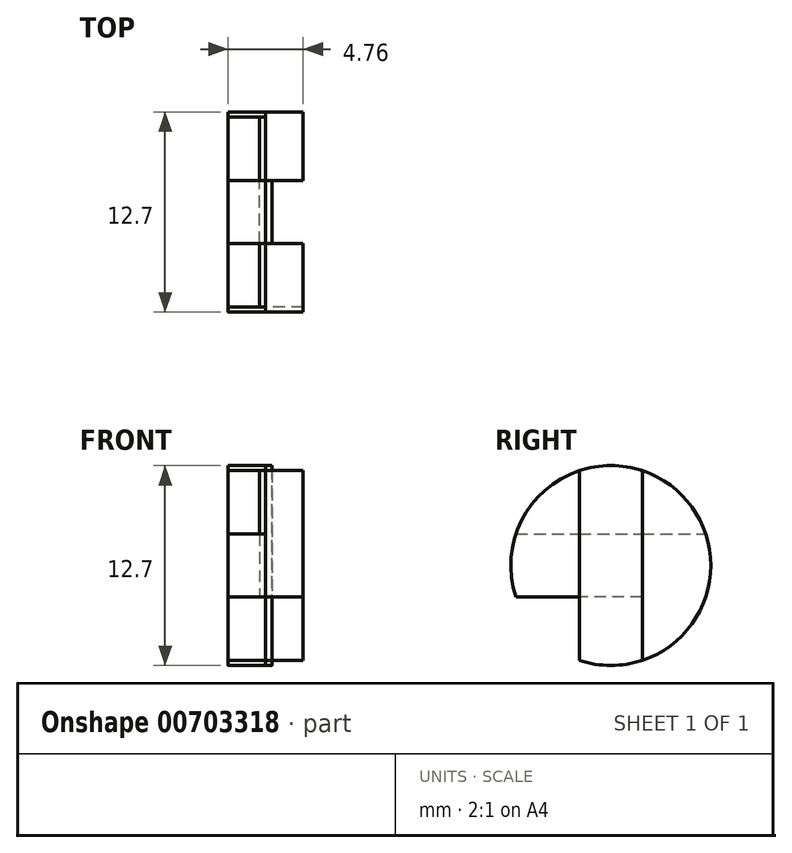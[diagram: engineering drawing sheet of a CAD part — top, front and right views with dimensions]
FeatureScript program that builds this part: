
annotation { "Feature Type Name" : "Feature", "Feature Type Description" : "" }
export const myFeature = defineFeature(function(context is Context, id is Id, definition is map)
    precondition{}
    {
        {
            var Q0;
            Q0=qCreatedBy(makeId("Right.planeOp"),FACE);
            var sketch = newSketch(context, id + "F0", { "sketchPlane" : qUnion([Q0])});
            skCircle(sketch, "E0", {"center": v(0, 0) * mm, "radius": 6.35 * mm});
            skLineSegment(sketch, "E1", {"start": v(-6.03, 2) * mm, "end": v(6.03, 2) * mm});
            skLineSegment(sketch, "E2", {"start": v(6.26, -2) * mm, "end": v(-6.03, -2) * mm});
            skLineSegment(sketch, "E3", {"start": v(-2, 6.03) * mm, "end": v(-2, -6.03) * mm});
            skLineSegment(sketch, "E4", {"start": v(2, -6.03) * mm, "end": v(2, 6.03) * mm});
            skSolve(sketch);
        }
        {
            var Q0;
            {var subQ0=sQuery(id+"F0.wireOp",EDGE,"E1");var subQ1=sQuery(id+"F0.wireOp",EDGE,"E0");var subQ2=makeQuery(id+"F0.imprint","INTERSECT",VERTEX,{"disambiguationData":[OD(0.0)],"derivedFrom":[subQ1,subQ0]});Q0=makeQuery(id+"F0.imprint","IMPRINT",FACE,{"disambiguationData":[TD([[makeQuery(id+"F0.imprint","IMPRINT",EDGE,{"disambiguationData":[TD([[subQ2,1.0]])],"derivedFrom":subQ1}),1.0]])]});}
            var Q1;
            {var subQ0=sQuery(id+"F0.wireOp",EDGE,"E1");var subQ1=sQuery(id+"F0.wireOp",EDGE,"E0");var subQ2=makeQuery(id+"F0.imprint","INTERSECT",VERTEX,{"disambiguationData":[OD(1.0)],"derivedFrom":[subQ1,subQ0]});Q1=makeQuery(id+"F0.imprint","IMPRINT",FACE,{"disambiguationData":[TD([[makeQuery(id+"F0.imprint","IMPRINT",EDGE,{"disambiguationData":[TD([[subQ2,-1.0]])],"derivedFrom":subQ1}),1.0]])]});}
            var Q2;
            {var subQ0=sQuery(id+"F0.wireOp",EDGE,"E1");var subQ1=sQuery(id+"F0.wireOp",EDGE,"E0");var subQ2=makeQuery(id+"F0.imprint","INTERSECT",VERTEX,{"disambiguationData":[OD(1.0)],"derivedFrom":[subQ1,subQ0]});Q2=makeQuery(id+"F0.imprint","IMPRINT",FACE,{"disambiguationData":[TD([[makeQuery(id+"F0.imprint","IMPRINT",EDGE,{"disambiguationData":[TD([[subQ2,1.0]])],"derivedFrom":subQ1}),1.0]])]});}
            var Q3;
            {var subQ0=sQuery(id+"F0.wireOp",EDGE,"E4");var subQ1=sQuery(id+"F0.wireOp",EDGE,"E0");var subQ2=makeQuery(id+"F0.imprint","INTERSECT",VERTEX,{"disambiguationData":[OD(0.0)],"derivedFrom":[subQ1,subQ0]});Q3=makeQuery(id+"F0.imprint","IMPRINT",FACE,{"disambiguationData":[TD([[makeQuery(id+"F0.imprint","IMPRINT",EDGE,{"disambiguationData":[TD([[subQ2,-1.0]])],"derivedFrom":subQ1}),1.0]])]});}
            var Q4;
            {var subQ0=sQuery(id+"F0.wireOp",EDGE,"E2");var subQ1=sQuery(id+"F0.wireOp",EDGE,"E0");var subQ2=makeQuery(id+"F0.imprint","INTERSECT",VERTEX,{"disambiguationData":[OD(0.0)],"derivedFrom":[subQ1,subQ0]});Q4=makeQuery(id+"F0.imprint","IMPRINT",FACE,{"disambiguationData":[TD([[makeQuery(id+"F0.imprint","IMPRINT",EDGE,{"disambiguationData":[TD([[subQ2,-1.0]])],"derivedFrom":subQ1}),1.0]])]});}
            var Q5;
            {var subQ0=sQuery(id+"F0.wireOp",EDGE,"E1");var subQ1=sQuery(id+"F0.wireOp",EDGE,"E0");var subQ2=makeQuery(id+"F0.imprint","INTERSECT",VERTEX,{"disambiguationData":[OD(0.0)],"derivedFrom":[subQ1,subQ0]});Q5=makeQuery(id+"F0.imprint","IMPRINT",FACE,{"disambiguationData":[TD([[makeQuery(id+"F0.imprint","IMPRINT",EDGE,{"disambiguationData":[TD([[subQ2,-1.0]])],"derivedFrom":subQ1}),1.0]])]});}
            extrude(context, id + "F1", {"entities" : qUnion([Q0, Q1, Q2, Q3, Q4, Q5]), "depth" : 2.38 * mm, "offsetDistance" : 25 * mm});
        }
        {
            var Q0;
            {var subQ0=sQuery(id+"F0.wireOp",EDGE,"E3");var subQ1=sQuery(id+"F0.wireOp",EDGE,"E0");var subQ2=makeQuery(id+"F0.imprint","INTERSECT",VERTEX,{"disambiguationData":[OD(0.0)],"derivedFrom":[subQ1,subQ0]});Q0=makeQuery(id+"F0.imprint","IMPRINT",FACE,{"disambiguationData":[TD([[makeQuery(id+"F0.imprint","IMPRINT",EDGE,{"disambiguationData":[TD([[subQ2,1.0]])],"derivedFrom":subQ1}),1.0]])]});}
            var Q1;
            {var subQ0=sQuery(id+"F0.wireOp",EDGE,"E3");var subQ1=sQuery(id+"F0.wireOp",EDGE,"E1");var subQ2=makeQuery(id+"F0.imprint","INTERSECT",VERTEX,{"derivedFrom":[subQ1,subQ0]});Q1=makeQuery(id+"F0.imprint","IMPRINT",FACE,{"disambiguationData":[TD([[makeQuery(id+"F0.imprint","IMPRINT",EDGE,{"disambiguationData":[TD([[subQ2,-1.0]])],"derivedFrom":subQ1}),-1.0]])]});}
            var Q2;
            {var subQ0=sQuery(id+"F0.wireOp",EDGE,"E3");var subQ1=sQuery(id+"F0.wireOp",EDGE,"E0");var subQ2=makeQuery(id+"F0.imprint","INTERSECT",VERTEX,{"disambiguationData":[OD(1.0)],"derivedFrom":[subQ1,subQ0]});Q2=makeQuery(id+"F0.imprint","IMPRINT",FACE,{"disambiguationData":[TD([[makeQuery(id+"F0.imprint","IMPRINT",EDGE,{"disambiguationData":[TD([[subQ2,-1.0]])],"derivedFrom":subQ1}),1.0]])]});}
            extrude(context, id + "F2", {"entities" : qUnion([Q0, Q1, Q2]), "depth" : 0.4 * mm, "offsetDistance" : 25 * mm});
        }
        {
            var Q0;
            {var subQ0=sQuery(id+"F0.wireOp",EDGE,"E1");var subQ1=sQuery(id+"F0.wireOp",EDGE,"E0");var subQ2=makeQuery(id+"F0.imprint","INTERSECT",VERTEX,{"disambiguationData":[OD(1.0)],"derivedFrom":[subQ1,subQ0]});Q0=makeQuery(id+"F0.imprint","IMPRINT",FACE,{"disambiguationData":[TD([[makeQuery(id+"F0.imprint","IMPRINT",EDGE,{"disambiguationData":[TD([[subQ2,-1.0]])],"derivedFrom":subQ1}),1.0]])]});}
            var Q1;
            {var subQ0=sQuery(id+"F0.wireOp",EDGE,"E3");var subQ1=sQuery(id+"F0.wireOp",EDGE,"E0");var subQ2=makeQuery(id+"F0.imprint","INTERSECT",VERTEX,{"disambiguationData":[OD(0.0)],"derivedFrom":[subQ1,subQ0]});Q1=makeQuery(id+"F0.imprint","IMPRINT",FACE,{"disambiguationData":[TD([[makeQuery(id+"F0.imprint","IMPRINT",EDGE,{"disambiguationData":[TD([[subQ2,1.0]])],"derivedFrom":subQ1}),1.0]])]});}
            var Q2;
            {var subQ0=sQuery(id+"F0.wireOp",EDGE,"E1");var subQ1=sQuery(id+"F0.wireOp",EDGE,"E0");var subQ2=makeQuery(id+"F0.imprint","INTERSECT",VERTEX,{"disambiguationData":[OD(0.0)],"derivedFrom":[subQ1,subQ0]});Q2=makeQuery(id+"F0.imprint","IMPRINT",FACE,{"disambiguationData":[TD([[makeQuery(id+"F0.imprint","IMPRINT",EDGE,{"disambiguationData":[TD([[subQ2,1.0]])],"derivedFrom":subQ1}),1.0]])]});}
            var Q3;
            {var subQ0=sQuery(id+"F0.wireOp",EDGE,"E2");var subQ1=sQuery(id+"F0.wireOp",EDGE,"E0");var subQ2=makeQuery(id+"F0.imprint","INTERSECT",VERTEX,{"disambiguationData":[OD(0.0)],"derivedFrom":[subQ1,subQ0]});Q3=makeQuery(id+"F0.imprint","IMPRINT",FACE,{"disambiguationData":[TD([[makeQuery(id+"F0.imprint","IMPRINT",EDGE,{"disambiguationData":[TD([[subQ2,-1.0]])],"derivedFrom":subQ1}),1.0]])]});}
            var Q4;
            {var subQ0=sQuery(id+"F0.wireOp",EDGE,"E3");var subQ1=sQuery(id+"F0.wireOp",EDGE,"E0");var subQ2=makeQuery(id+"F0.imprint","INTERSECT",VERTEX,{"disambiguationData":[OD(1.0)],"derivedFrom":[subQ1,subQ0]});Q4=makeQuery(id+"F0.imprint","IMPRINT",FACE,{"disambiguationData":[TD([[makeQuery(id+"F0.imprint","IMPRINT",EDGE,{"disambiguationData":[TD([[subQ2,-1.0]])],"derivedFrom":subQ1}),1.0]])]});}
            var Q5;
            {var subQ0=sQuery(id+"F0.wireOp",EDGE,"E4");var subQ1=sQuery(id+"F0.wireOp",EDGE,"E0");var subQ2=makeQuery(id+"F0.imprint","INTERSECT",VERTEX,{"disambiguationData":[OD(0.0)],"derivedFrom":[subQ1,subQ0]});Q5=makeQuery(id+"F0.imprint","IMPRINT",FACE,{"disambiguationData":[TD([[makeQuery(id+"F0.imprint","IMPRINT",EDGE,{"disambiguationData":[TD([[subQ2,-1.0]])],"derivedFrom":subQ1}),1.0]])]});}
            extrude(context, id + "F3", {"entities" : qUnion([Q0, Q1, Q2, Q3, Q4, Q5]), "oppositeDirection" : true, "depth" : 2.38 * mm, "offsetDistance" : 25 * mm});
        }
        {
            var Q0;
            {var subQ0=sQuery(id+"F0.wireOp",EDGE,"E1");var subQ1=sQuery(id+"F0.wireOp",EDGE,"E0");var subQ2=makeQuery(id+"F0.imprint","INTERSECT",VERTEX,{"disambiguationData":[OD(1.0)],"derivedFrom":[subQ1,subQ0]});Q0=makeQuery(id+"F0.imprint","IMPRINT",FACE,{"disambiguationData":[TD([[makeQuery(id+"F0.imprint","IMPRINT",EDGE,{"disambiguationData":[TD([[subQ2,1.0]])],"derivedFrom":subQ1}),1.0]])]});}
            var Q1;
            {var subQ0=sQuery(id+"F0.wireOp",EDGE,"E3");var subQ1=sQuery(id+"F0.wireOp",EDGE,"E1");var subQ2=makeQuery(id+"F0.imprint","INTERSECT",VERTEX,{"derivedFrom":[subQ1,subQ0]});Q1=makeQuery(id+"F0.imprint","IMPRINT",FACE,{"disambiguationData":[TD([[makeQuery(id+"F0.imprint","IMPRINT",EDGE,{"disambiguationData":[TD([[subQ2,-1.0]])],"derivedFrom":subQ1}),-1.0]])]});}
            var Q2;
            {var subQ0=sQuery(id+"F0.wireOp",EDGE,"E1");var subQ1=sQuery(id+"F0.wireOp",EDGE,"E0");var subQ2=makeQuery(id+"F0.imprint","INTERSECT",VERTEX,{"disambiguationData":[OD(0.0)],"derivedFrom":[subQ1,subQ0]});Q2=makeQuery(id+"F0.imprint","IMPRINT",FACE,{"disambiguationData":[TD([[makeQuery(id+"F0.imprint","IMPRINT",EDGE,{"disambiguationData":[TD([[subQ2,-1.0]])],"derivedFrom":subQ1}),1.0]])]});}
            extrude(context, id + "F4", {"entities" : qUnion([Q0, Q1, Q2]), "oppositeDirection" : true, "depth" : 0.4 * mm, "offsetDistance" : 25 * mm});
        }
    });
